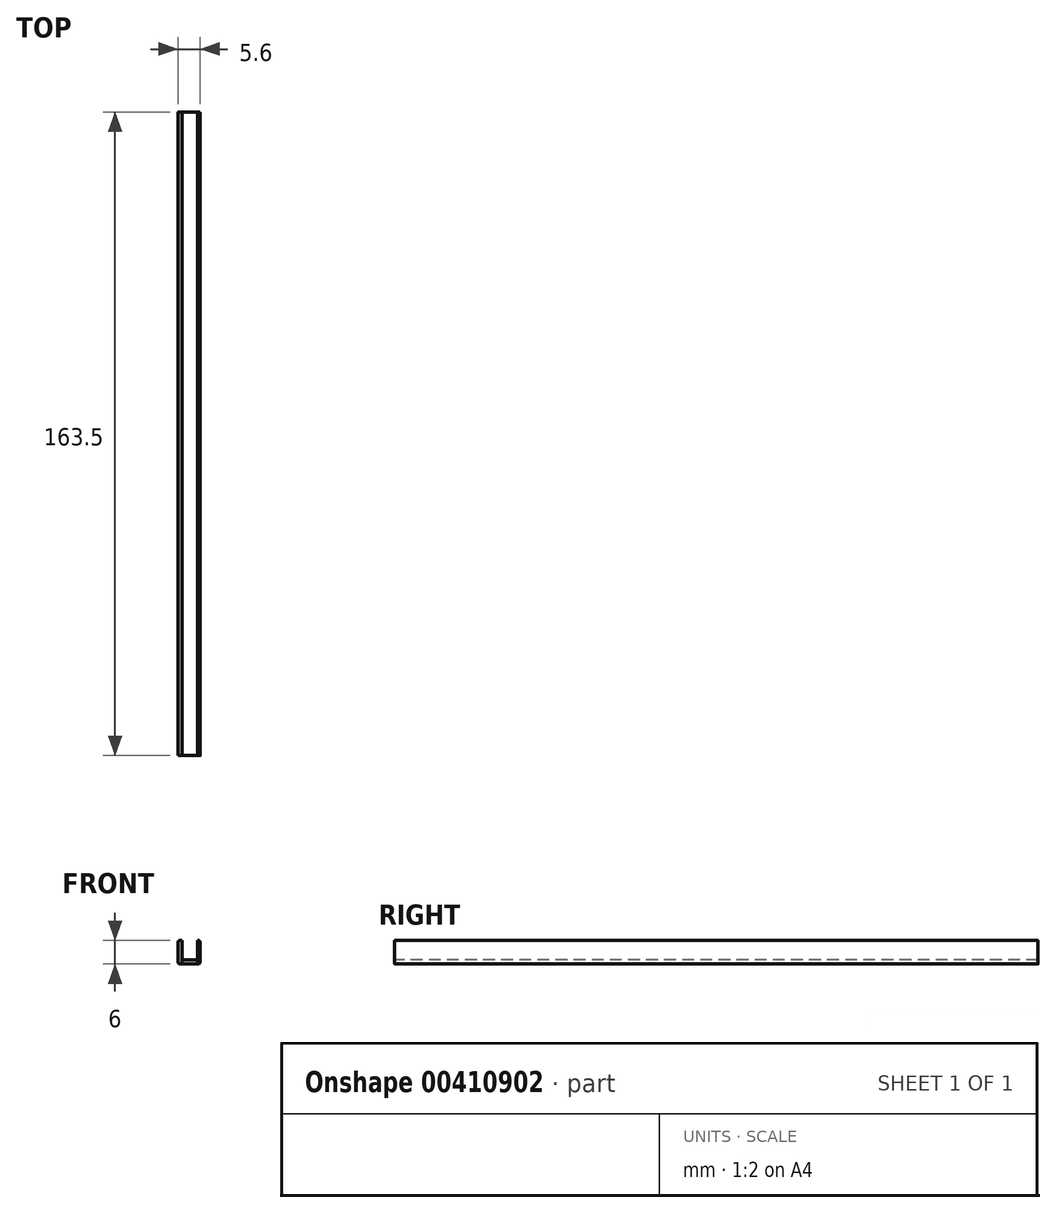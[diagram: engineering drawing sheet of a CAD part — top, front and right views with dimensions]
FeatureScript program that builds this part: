
annotation { "Feature Type Name" : "Feature", "Feature Type Description" : "" }
export const myFeature = defineFeature(function(context is Context, id is Id, definition is map)
    precondition{}
    {
        {
            var Q0;
            Q0=qCreatedBy(makeId("Top.planeOp"),FACE);
            var sketch = newSketch(context, id + "F0", { "sketchPlane" : qUnion([Q0])});
            skLineSegment(sketch, "E0.bottom", {"start": v(-2.95, 143.5) * mm, "end": v(2.65, 143.5) * mm});
            skLineSegment(sketch, "E0.top", {"start": v(-2.95, -20) * mm, "end": v(2.65, -20) * mm});
            skLineSegment(sketch, "E0.left", {"start": v(-2.95, 143.5) * mm, "end": v(-2.95, -20) * mm});
            skLineSegment(sketch, "E0.right", {"start": v(2.65, 143.5) * mm, "end": v(2.65, -20) * mm});
            skPoint(sketch, "E0.middle", {"position": v(0, 0) * mm});
            skLineSegment(sketch, "E1", {"start": v(-1.95, 143.5) * mm, "end": v(-1.95, -20) * mm});
            skLineSegment(sketch, "E2.MirrorCS", {"start": v(1.95, 143.5) * mm, "end": v(1.95, -20) * mm});
            skSolve(sketch);
        }
        {
            var Q0;
            {var subQ0=sQuery(id+"F0.wireOp",EDGE,"E0.left");Q0=makeQuery(id+"F0.imprint","IMPRINT",FACE,{"disambiguationData":[TD([[makeQuery(id+"F0.imprint","IMPRINT",EDGE,{"derivedFrom":subQ0}),1.0]])]});}
            var Q1;
            {var subQ0=sQuery(id+"F0.wireOp",EDGE,"E0.right");Q1=makeQuery(id+"F0.imprint","IMPRINT",FACE,{"disambiguationData":[TD([[makeQuery(id+"F0.imprint","IMPRINT",EDGE,{"derivedFrom":subQ0}),-1.0]])]});}
            extrude(context, id + "F1", {"entities" : qUnion([Q0, Q1]), "depth" : 6 * mm});
        }
        {
            var Q0;
            Q0=makeQuery(id+"F1.opExtrude","CAP_EDGE",EDGE,{"disambiguationData":[OSD([sQuery(id+"F0.wireOp",EDGE,"E0.left")])],"isStart":false});
            var Q1;
            Q1=makeQuery(id+"F1.opExtrude","CAP_EDGE",EDGE,{"disambiguationData":[OSD([sQuery(id+"F0.wireOp",EDGE,"E0.right")])],"isStart":false});
            var Q2;
            Q2=makeQuery(id+"F1.opExtrude","CAP_EDGE",EDGE,{"disambiguationData":[OSD([sQuery(id+"F0.wireOp",EDGE,"E0.left")])],"isStart":true});
            var Q3;
            Q3=makeQuery(id+"F1.opExtrude","CAP_EDGE",EDGE,{"disambiguationData":[OSD([sQuery(id+"F0.wireOp",EDGE,"E0.right")])],"isStart":true});
            fillet(context, id + "F2", {"entities" : qUnion([Q0, Q1, Q2, Q3]), "radius" : .5 * mm, "tangentPropagation" : true, "allowEdgeOverflow" : false});
        }
        {
            var Q0;
            {var subQ0=sQuery(id+"F0.wireOp",EDGE,"E1");Q0=makeQuery(id+"F0.imprint","IMPRINT",FACE,{"disambiguationData":[TD([[makeQuery(id+"F0.imprint","IMPRINT",EDGE,{"derivedFrom":subQ0}),1.0]])]});}
            extrude(context, id + "F3", {"entities" : qUnion([Q0]), "depth" : 1 * mm});
        }
    });
